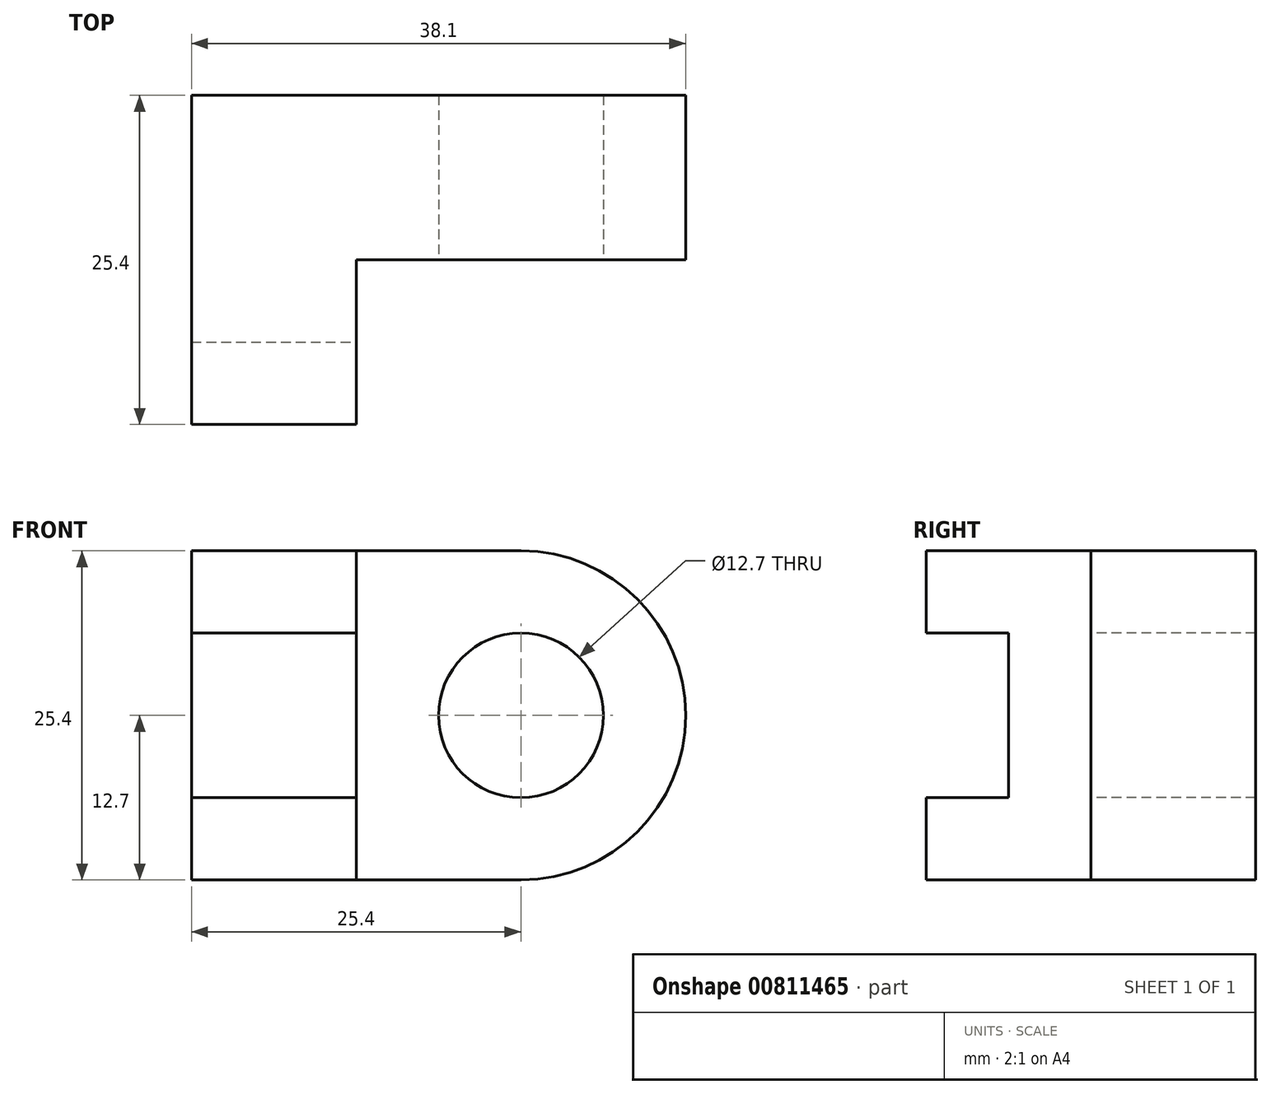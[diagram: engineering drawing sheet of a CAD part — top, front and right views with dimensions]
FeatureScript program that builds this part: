
annotation { "Feature Type Name" : "Feature", "Feature Type Description" : "" }
export const myFeature = defineFeature(function(context is Context, id is Id, definition is map)
    precondition{}
    {
        {
            var Q0;
            Q0=qCreatedBy(makeId("Top.planeOp"),FACE);
            var sketch = newSketch(context, id + "F0", { "sketchPlane" : qUnion([Q0])});
            skLineSegment(sketch, "E0", {"start": v(0, 0) * mm, "end": v(0, 25.4) * mm});
            skLineSegment(sketch, "E1", {"start": v(0, 25.4) * mm, "end": v(25.4, 25.4) * mm});
            skLineSegment(sketch, "E2", {"start": v(25.4, 25.4) * mm, "end": v(25.4, 0) * mm});
            skLineSegment(sketch, "E3", {"start": v(25.4, 0) * mm, "end": v(0, 0) * mm});
            skSolve(sketch);
        }
        {
            var Q0;
            Q0 = qSketchRegion(id + "F0", true);
            extrude(context, id + "F1", {"entities" : qUnion([Q0]), "depth" : 25.4 * mm, "offsetDistance" : 25.4 * mm});
        }
        {
            var Q0;
            Q0=makeQuery(id+"F1.opExtrude","SWEPT_FACE",FACE,{"disambiguationData":[OSD([sQuery(id+"F0.wireOp",EDGE,"E3")])]});
            var sketch = newSketch(context, id + "F2", { "sketchPlane" : qUnion([Q0])});
            skLineSegment(sketch, "E4", {"start": v(0, 0) * mm, "end": v(0, 6.35) * mm, "construction": true});
            skLineSegment(sketch, "E5", {"start": v(0, 6.35) * mm, "end": v(12.7, 6.35) * mm});
            skLineSegment(sketch, "E6", {"start": v(12.7, 6.35) * mm, "end": v(12.7, 19.05) * mm});
            skLineSegment(sketch, "E7", {"start": v(12.7, 19.05) * mm, "end": v(0, 19.05) * mm});
            skSolve(sketch);
        }
        {
            var Q0;
            Q0 = qSketchRegion(id + "F2", true);
            var Q1;
            {var subQ0=sQuery(id+"F2.wireOp",EDGE,"E5");Q1=makeQuery(id+"F2.imprint","IMPRINT",FACE,{"disambiguationData":[TD([[makeQuery(id+"F2.imprint","IMPRINT",EDGE,{"derivedFrom":subQ0}),1.0]])]});}
            extrude(context, id + "F3", {"entities" : qUnion([Q0, Q1]), "operationType" : NewBodyOperationType.REMOVE, "oppositeDirection" : true, "depth" : 6.35 * mm, "offsetDistance" : 25.4 * mm});
        }
        {
            var Q0;
            Q0=makeQuery(id+"F1.opExtrude","SWEPT_FACE",FACE,{"disambiguationData":[OSD([sQuery(id+"F0.wireOp",EDGE,"E3")])]});
            var sketch = newSketch(context, id + "F4", { "sketchPlane" : qUnion([Q0])});
            skLineSegment(sketch, "E8", {"start": v(12.7, 19.05) * mm, "end": v(12.7, 25.4) * mm});
            skLineSegment(sketch, "E9", {"start": v(12.7, 6.35) * mm, "end": v(12.7, 0) * mm});
            skSolve(sketch);
        }
        {
            var Q0;
            Q0 = qSketchRegion(id + "F4", true);
            var Q1;
            {var subQ3=sQuery(id+"F4.wireOp",EDGE,"E8");Q1=makeQuery(id+"F4.imprint","IMPRINT",FACE,{"disambiguationData":[TD([[makeQuery(id+"F4.imprint","IMPRINT",EDGE,{"derivedFrom":subQ3}),-1.0]])]});}
            extrude(context, id + "F5", {"entities" : qUnion([Q0, Q1]), "operationType" : NewBodyOperationType.REMOVE, "oppositeDirection" : true, "depth" : 12.7 * mm, "offsetDistance" : 25.4 * mm});
        }
        {
            var Q0;
            Q0=makeQuery(id+"F5.boolean.opBoolean","COPY",FACE,{"derivedFrom":makeQuery(id+"F5.opExtrude","CAP_FACE",FACE,{"disambiguationData":[OSD([sQuery(id+"F0.wireOp",EDGE,"E2"),sQuery(id+"F0.wireOp",EDGE,"E3"),sQuery(id+"F2.wireOp",EDGE,"E6"),sQuery(id+"F4.wireOp",EDGE,"E8"),sQuery(id+"F4.wireOp",EDGE,"E9")])],"isStart":false})});
            var sketch = newSketch(context, id + "F6", { "sketchPlane" : qUnion([Q0])});
            skArc(sketch, "E10", {"start": v(25.4, 0) * mm, "mid": v(38.1, 12.7) * mm, "end": v(25.4, 25.4) * mm});
            skSolve(sketch);
        }
        {
            var Q0;
            Q0 = qSketchRegion(id + "F6", true);
            var Q1;
            Q1=makeQuery(id+"F6.imprint","IMPRINT",FACE,{"disambiguationData":[TD([[makeQuery(id+"F6.imprint","IMPRINT",EDGE,{"derivedFrom":sQuery(id+"F6.wireOp",EDGE,"E10")}),1.0]])]});
            extrude(context, id + "F7", {"entities" : qUnion([Q0, Q1]), "operationType" : NewBodyOperationType.ADD, "oppositeDirection" : true, "depth" : 12.7 * mm, "offsetDistance" : 25.4 * mm});
        }
        {
            var Q0;
            {var subQ0=sQuery(id+"F0.wireOp",EDGE,"E3");var subQ1=sQuery(id+"F0.wireOp",EDGE,"E2");Q0=makeQuery(id+"F7.boolean.opBoolean","MERGE",FACE,{"derivedFrom":[makeQuery(id+"F5.boolean.opBoolean","COPY",FACE,{"derivedFrom":makeQuery(id+"F5.opExtrude","CAP_FACE",FACE,{"disambiguationData":[OSD([subQ1,subQ0,sQuery(id+"F2.wireOp",EDGE,"E6"),sQuery(id+"F4.wireOp",EDGE,"E8"),sQuery(id+"F4.wireOp",EDGE,"E9")])],"isStart":false})}),makeQuery(id+"F7.opExtrude","CAP_FACE",FACE,{"disambiguationData":[OSD([subQ1,subQ0,sQuery(id+"F6.wireOp",EDGE,"E10")])],"isStart":true})]});}
            var sketch = newSketch(context, id + "F8", { "sketchPlane" : qUnion([Q0])});
            skLineSegment(sketch, "E11", {"start": v(12.7, 12.7) * mm, "end": v(25.4, 12.7) * mm, "construction": true});
            skCircle(sketch, "E12", {"center": v(25.4, 12.7) * mm, "radius": 6.35 * mm});
            skSolve(sketch);
        }
        {
            var Q0;
            Q0=makeQuery(id+"F8.imprint","IMPRINT",FACE,{"disambiguationData":[TD([[makeQuery(id+"F8.imprint","IMPRINT",EDGE,{"derivedFrom":sQuery(id+"F8.wireOp",EDGE,"E12")}),1.0]])]});
            extrude(context, id + "F9", {"entities" : qUnion([Q0]), "operationType" : NewBodyOperationType.REMOVE, "oppositeDirection" : true, "depth" : 25.4 * mm, "offsetDistance" : 25.4 * mm});
        }
    });
